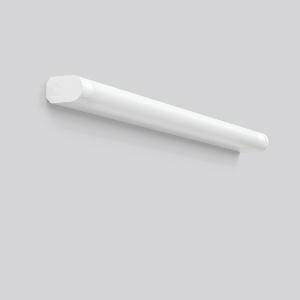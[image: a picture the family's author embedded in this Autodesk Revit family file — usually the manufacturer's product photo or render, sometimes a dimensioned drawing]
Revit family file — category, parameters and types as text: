
# Revit family: rt_44_451175_002_c338
name_source: partatom
category: Lighting Fixtures
units: mm (PartAtom-declared; Revit-internal decimal feet)

## family parameters
Cut with Voids When Loaded = No
Host = Face
Light Source = No
Part Type = Normal
Room Calculation Point = No
Round Connector Dimension = Use Diameter
Shared = No

## types (1)
- RT 44 (1 x LED Modul 830, 1400 lm, 3000)
    Apparent Load = 15 VA
    CIE Flux Codes = 36 65 85 82 100
    Color Rendering = 80
    Color Temperature = 3000
    Default Elevation = 1800 mm
    Description = Series: RT 44
Linear luminaire, can be used as wall and mirror luminaire. Base: aluminium, powder-coated. End caps: plastic (polycarbonate), shock-resistant. Diffuser: plastic (polycarbonate), opal. Suitable for Ceiling mounting, Wall (surface). Can be installed horizontally and vertically. Very easy installation thanks to Plug+Play connection. With push button switch and Schukoplug socket. Driver integrated. High type of protection: IP44 for use in wet areas. 
Colour: pure white (RAL 9010)
Length: 1021 mm
Width: 55 mm
Height: 87 mm
Lamp: LED
Socket: without socket
Colour temperature: 3000K
Colour rendering index (CRI): 80
System power: 15 W
Rated luminous flux: 1400 lm
Luminous efficiency: 93 lm/W
Control gear: Regulated power supply
Protection class: I
Type of protection: IP 44
    Height = 87 mm
    Lamp = 1 x LED Modul 830
    Lamp Light Flux = 1400 lm
    Lamp count = 1
    Length = 1021 mm
    Lifetime = 50000 h
    Luminous efficacy = 93 lm/W
    Manufacturer = RZB
    ModVariant = No
    Model = 451175.002
    Mounting Place = Ceiling, Wall
    Mounting Type = Surface mounted
    Number of Poles = 1
    OnlyDefault = Yes
    Power Factor = 1
    Product Name = RT 44
    Product group = Surface mounted ceiling and wall luminaires
    ProductGroupID = 305
    Protection Class = Protection class I
    Protection Degree = IP 44
    RLX_Detail_Level = 1
    RLX_Emergency_Light_Flux = 0 lm
    RLX_Emergency_Type = 0
    RLX_Emergency_Type_DB = No
    RlxData = <blob elided: 27733 chars, md5=20032361>
    Socket = socket
    Standby Power = 0 W
    System Light Flux = 1400 lm
    System Power = 15 W
    Type Comments = Product without accessories
    Type Image = 451061.752.jpg
    URL = http://relux.com
    VarID = ---
    Voltage = 230 V
    Voltage Range = 220-240 V
    Weight = 0.00 kg
    Width = 55 mm

## geometry (parser evidence)
native form markers: Blend x4, Sweep x12
no freeform markers — native parametric forms only
